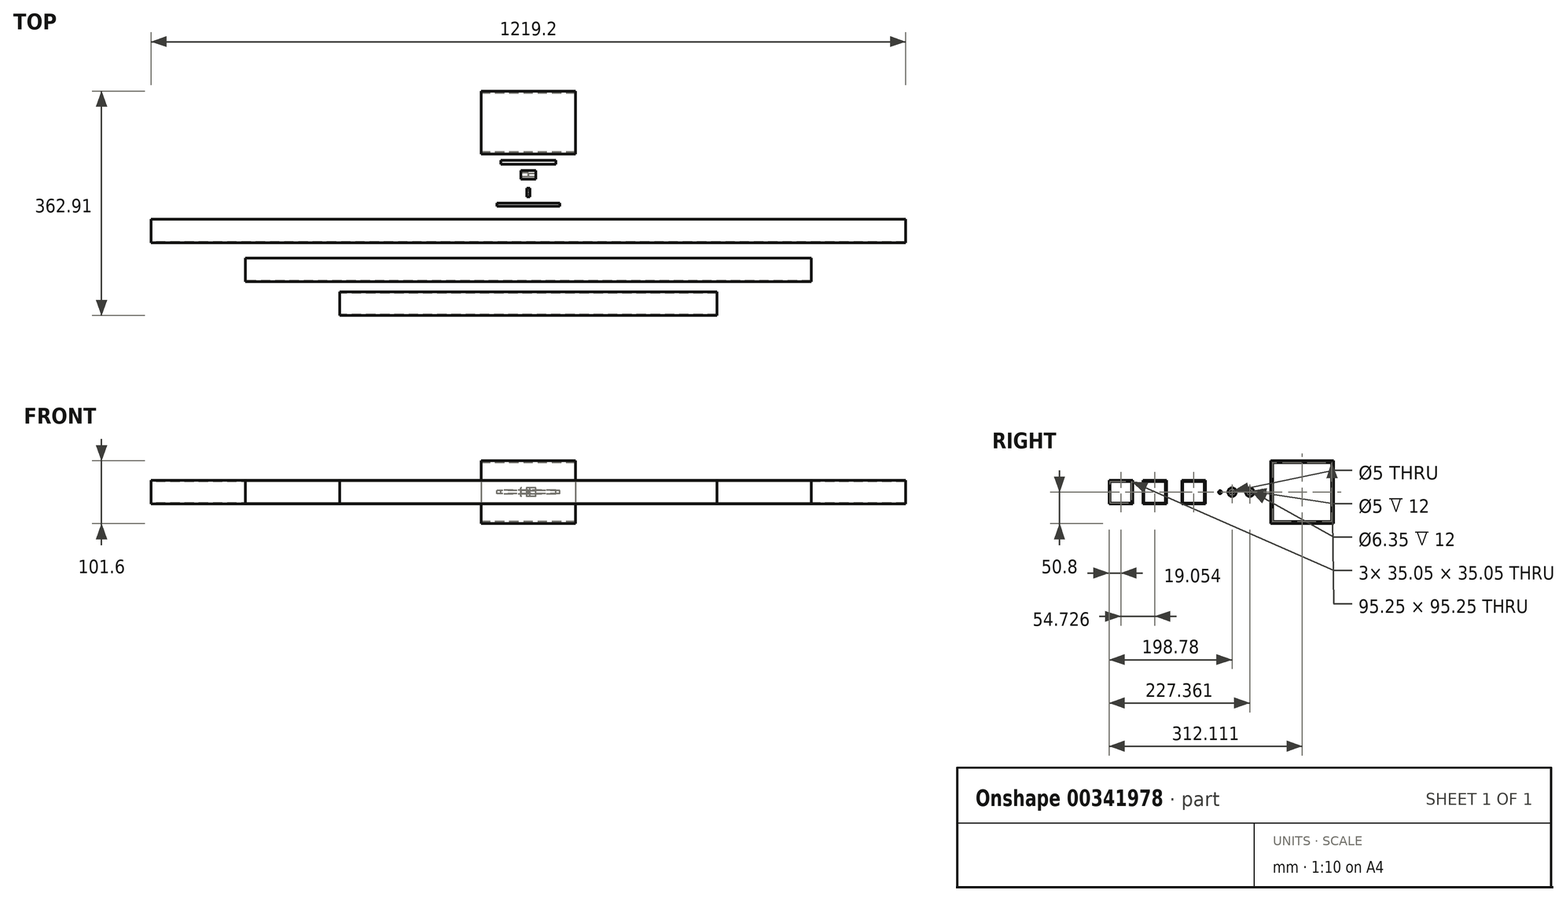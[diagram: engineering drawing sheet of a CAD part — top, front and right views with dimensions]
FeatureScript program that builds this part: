
annotation { "Feature Type Name" : "Feature", "Feature Type Description" : "" }
export const myFeature = defineFeature(function(context is Context, id is Id, definition is map)
    precondition{}
    {
        {
            var Q0;
            Q0=qCreatedBy(makeId("Right.planeOp"),FACE);
            var sketch = newSketch(context, id + "F0", { "sketchPlane" : qUnion([Q0])});
            skLineSegment(sketch, "E0.bottom", {"start": v(-81.24, 19.05) * mm, "end": v(-43.14, 19.05) * mm});
            skLineSegment(sketch, "E0.top", {"start": v(-81.24, -19.05) * mm, "end": v(-43.14, -19.05) * mm});
            skLineSegment(sketch, "E0.left", {"start": v(-81.24, 19.05) * mm, "end": v(-81.24, -19.05) * mm});
            skLineSegment(sketch, "E0.right", {"start": v(-43.14, 19.05) * mm, "end": v(-43.14, -19.05) * mm});
            skPoint(sketch, "E0.middle", {"position": v(-62.19, 0) * mm});
            skLineSegment(sketch, "E1.0", {"start": v(-44.66, 17.53) * mm, "end": v(-44.66, -17.53) * mm});
            skLineSegment(sketch, "E1.1", {"start": v(-79.71, 17.53) * mm, "end": v(-44.66, 17.53) * mm});
            skLineSegment(sketch, "E1.2", {"start": v(-79.71, 17.53) * mm, "end": v(-79.71, -17.53) * mm});
            skLineSegment(sketch, "E1.3", {"start": v(-79.71, -17.53) * mm, "end": v(-44.66, -17.53) * mm});
            skLineSegment(sketch, "E2.bottom", {"start": v(-144.05, 19.05) * mm, "end": v(-105.95, 19.05) * mm});
            skLineSegment(sketch, "E2.top", {"start": v(-144.05, -19.05) * mm, "end": v(-105.95, -19.05) * mm});
            skLineSegment(sketch, "E2.left", {"start": v(-144.05, 19.05) * mm, "end": v(-144.05, -19.05) * mm});
            skLineSegment(sketch, "E2.right", {"start": v(-105.95, 19.05) * mm, "end": v(-105.95, -19.05) * mm});
            skPoint(sketch, "E2.middle", {"position": v(-125, 0) * mm});
            skLineSegment(sketch, "E3.0", {"start": v(-107.47, 17.53) * mm, "end": v(-107.47, -17.53) * mm});
            skLineSegment(sketch, "E3.1", {"start": v(-142.53, 17.53) * mm, "end": v(-107.47, 17.53) * mm});
            skLineSegment(sketch, "E3.2", {"start": v(-142.53, 17.53) * mm, "end": v(-142.53, -17.53) * mm});
            skLineSegment(sketch, "E3.3", {"start": v(-142.53, -17.53) * mm, "end": v(-107.47, -17.53) * mm});
            skLineSegment(sketch, "E4.bottom", {"start": v(-198.78, 19.05) * mm, "end": v(-160.68, 19.05) * mm});
            skLineSegment(sketch, "E4.top", {"start": v(-198.78, -19.05) * mm, "end": v(-160.68, -19.05) * mm});
            skLineSegment(sketch, "E4.left", {"start": v(-198.78, 19.05) * mm, "end": v(-198.78, -19.05) * mm});
            skLineSegment(sketch, "E4.right", {"start": v(-160.68, 19.05) * mm, "end": v(-160.68, -19.05) * mm});
            skPoint(sketch, "E4.middle", {"position": v(-179.73, 0) * mm});
            skLineSegment(sketch, "E5.0", {"start": v(-162.2, 17.53) * mm, "end": v(-162.2, -17.53) * mm});
            skLineSegment(sketch, "E5.1", {"start": v(-197.25, 17.53) * mm, "end": v(-162.2, 17.53) * mm});
            skLineSegment(sketch, "E5.2", {"start": v(-197.25, 17.53) * mm, "end": v(-197.25, -17.53) * mm});
            skLineSegment(sketch, "E5.3", {"start": v(-197.25, -17.53) * mm, "end": v(-162.2, -17.53) * mm});
            skSolve(sketch);
        }
        {
            var Q0;
            Q0=qCreatedBy(makeId("Right.planeOp"),FACE);
            var sketch = newSketch(context, id + "F1", { "sketchPlane" : qUnion([Q0])});
            skCircle(sketch, "E6", {"center": v(0, 0) * mm, "radius": 7 * mm});
            skCircle(sketch, "E7", {"center": v(0, 0) * mm, "radius": 2.5 * mm});
            skSolve(sketch);
        }
        {
            var Q0;
            Q0=qCreatedBy(makeId("Right.planeOp"),FACE);
            var sketch = newSketch(context, id + "F2", { "sketchPlane" : qUnion([Q0])});
            skCircle(sketch, "E8", {"center": v(-19.34, 0) * mm, "radius": 2.5 * mm});
            skSolve(sketch);
        }
        {
            var Q0;
            Q0=makeQuery(id+"F0.imprint","IMPRINT",FACE,{"disambiguationData":[TD([[makeQuery(id+"F0.imprint","IMPRINT",EDGE,{"derivedFrom":sQuery(id+"F0.wireOp",EDGE,"E0.bottom")}),-1.0]])]});
            extrude(context, id + "F3", {"entities" : qUnion([Q0]), "endBound" : BoundingType.SYMMETRIC, "depth" : 1219.2 * mm});
        }
        {
            var Q0;
            Q0=makeQuery(id+"F2.imprint","IMPRINT",FACE,{"disambiguationData":[TD([[makeQuery(id+"F2.imprint","IMPRINT",EDGE,{"derivedFrom":sQuery(id+"F2.wireOp",EDGE,"E8")}),1.0]])]});
            extrude(context, id + "F4", {"entities" : qUnion([Q0]), "endBound" : BoundingType.SYMMETRIC, "depth" : 101.6 * mm});
        }
        {
            var Q0;
            Q0=makeQuery(id+"F1.imprint","IMPRINT",FACE,{"disambiguationData":[TD([[makeQuery(id+"F1.imprint","IMPRINT",EDGE,{"derivedFrom":sQuery(id+"F1.wireOp",EDGE,"E6")}),1.0]])]});
            extrude(context, id + "F5", {"entities" : qUnion([Q0]), "endBound" : BoundingType.SYMMETRIC, "depth" : 5 * mm});
        }
        {
            var Q0;
            Q0=makeQuery(id+"F0.imprint","IMPRINT",FACE,{"disambiguationData":[TD([[makeQuery(id+"F0.imprint","IMPRINT",EDGE,{"derivedFrom":sQuery(id+"F0.wireOp",EDGE,"E2.bottom")}),-1.0]])]});
            extrude(context, id + "F6", {"entities" : qUnion([Q0]), "endBound" : BoundingType.SYMMETRIC, "depth" : 914.4 * mm});
        }
        {
            var Q0;
            Q0=makeQuery(id+"F0.imprint","IMPRINT",FACE,{"disambiguationData":[TD([[makeQuery(id+"F0.imprint","IMPRINT",EDGE,{"derivedFrom":sQuery(id+"F0.wireOp",EDGE,"E4.bottom")}),-1.0]])]});
            extrude(context, id + "F7", {"entities" : qUnion([Q0]), "endBound" : BoundingType.SYMMETRIC, "depth" : 609.6 * mm});
        }
        {
            var Q0;
            Q0=qCreatedBy(makeId("Right.planeOp"),FACE);
            var sketch = newSketch(context, id + "F8", { "sketchPlane" : qUnion([Q0])});
            skCircle(sketch, "E9", {"center": v(28.58, 0) * mm, "radius": 7 * mm});
            skSolve(sketch);
        }
        {
            var Q0;
            Q0=makeQuery(id+"F8.imprint","IMPRINT",FACE,{"disambiguationData":[TD([[makeQuery(id+"F8.imprint","IMPRINT",EDGE,{"derivedFrom":sQuery(id+"F8.wireOp",EDGE,"E9")}),1.0]])]});
            extrude(context, id + "F9", {"entities" : qUnion([Q0]), "endBound" : BoundingType.SYMMETRIC, "depth" : 24 * mm});
        }
        {
            var Q0;
            Q0=makeQuery(id+"F9.opExtrude","CAP_FACE",FACE,{"disambiguationData":[OSD([sQuery(id+"F8.wireOp",EDGE,"E9")])],"isStart":false});
            var sketch = newSketch(context, id + "F10", { "sketchPlane" : qUnion([Q0])});
            skCircle(sketch, "E10.0.0", {"center": v(28.58, 0) * mm, "radius": 7 * mm});
            skCircle(sketch, "E11", {"center": v(28.58, 0) * mm, "radius": 2.5 * mm});
            skSolve(sketch);
        }
        {
            var Q0;
            Q0=makeQuery(id+"F10.imprint","IMPRINT",FACE,{"disambiguationData":[TD([[makeQuery(id+"F10.imprint","IMPRINT",EDGE,{"derivedFrom":sQuery(id+"F10.wireOp",EDGE,"E11")}),1.0]])]});
            extrude(context, id + "F11", {"entities" : qUnion([Q0]), "operationType" : NewBodyOperationType.REMOVE, "oppositeDirection" : true, "depth" : 12 * mm});
        }
        {
            var Q0;
            Q0=makeQuery(id+"F9.opExtrude","CAP_FACE",FACE,{"disambiguationData":[OSD([sQuery(id+"F8.wireOp",EDGE,"E9")])],"isStart":true});
            var sketch = newSketch(context, id + "F12", { "sketchPlane" : qUnion([Q0])});
            skCircle(sketch, "E12.0.0", {"center": v(-28.58, 0) * mm, "radius": 7 * mm});
            skCircle(sketch, "E13", {"center": v(-28.58, 0) * mm, "radius": 3.18 * mm});
            skSolve(sketch);
        }
        {
            var Q0;
            Q0=makeQuery(id+"F12.imprint","IMPRINT",FACE,{"disambiguationData":[TD([[makeQuery(id+"F12.imprint","IMPRINT",EDGE,{"derivedFrom":sQuery(id+"F12.wireOp",EDGE,"E13")}),1.0]])]});
            extrude(context, id + "F13", {"entities" : qUnion([Q0]), "operationType" : NewBodyOperationType.REMOVE, "oppositeDirection" : true, "depth" : 12 * mm});
        }
        {
            var Q0;
            Q0=qCreatedBy(makeId("Right.planeOp"),FACE);
            var sketch = newSketch(context, id + "F14", { "sketchPlane" : qUnion([Q0])});
            skCircle(sketch, "E14", {"center": v(49, 0) * mm, "radius": 3.18 * mm});
            skSolve(sketch);
        }
        {
            var Q0;
            Q0=makeQuery(id+"F14.imprint","IMPRINT",FACE,{"disambiguationData":[TD([[makeQuery(id+"F14.imprint","IMPRINT",EDGE,{"derivedFrom":sQuery(id+"F14.wireOp",EDGE,"E14")}),1.0]])]});
            extrude(context, id + "F15", {"entities" : qUnion([Q0]), "endBound" : BoundingType.SYMMETRIC, "depth" : 88.9 * mm});
        }
        {
            var Q0;
            Q0=qCreatedBy(makeId("Right.planeOp"),FACE);
            var sketch = newSketch(context, id + "F16", { "sketchPlane" : qUnion([Q0])});
            skLineSegment(sketch, "E15.bottom", {"start": v(62.53, 50.8) * mm, "end": v(164.13, 50.8) * mm});
            skLineSegment(sketch, "E15.top", {"start": v(62.53, -50.8) * mm, "end": v(164.13, -50.8) * mm});
            skLineSegment(sketch, "E15.left", {"start": v(62.53, 50.8) * mm, "end": v(62.53, -50.8) * mm});
            skLineSegment(sketch, "E15.right", {"start": v(164.13, 50.8) * mm, "end": v(164.13, -50.8) * mm});
            skPoint(sketch, "E15.middle", {"position": v(113.33, 0) * mm});
            skLineSegment(sketch, "E16.0", {"start": v(65.7, 47.62) * mm, "end": v(65.7, -47.63) * mm});
            skLineSegment(sketch, "E16.1", {"start": v(65.7, 47.62) * mm, "end": v(160.96, 47.62) * mm});
            skLineSegment(sketch, "E16.2", {"start": v(160.96, 47.62) * mm, "end": v(160.96, -47.63) * mm});
            skLineSegment(sketch, "E16.3", {"start": v(65.7, -47.63) * mm, "end": v(160.96, -47.63) * mm});
            skSolve(sketch);
        }
        {
            var Q0;
            Q0=makeQuery(id+"F16.imprint","IMPRINT",FACE,{"disambiguationData":[TD([[makeQuery(id+"F16.imprint","IMPRINT",EDGE,{"derivedFrom":sQuery(id+"F16.wireOp",EDGE,"E15.bottom")}),-1.0]])]});
            extrude(context, id + "F17", {"entities" : qUnion([Q0]), "endBound" : BoundingType.SYMMETRIC, "depth" : 152.4 * mm});
        }
    });
